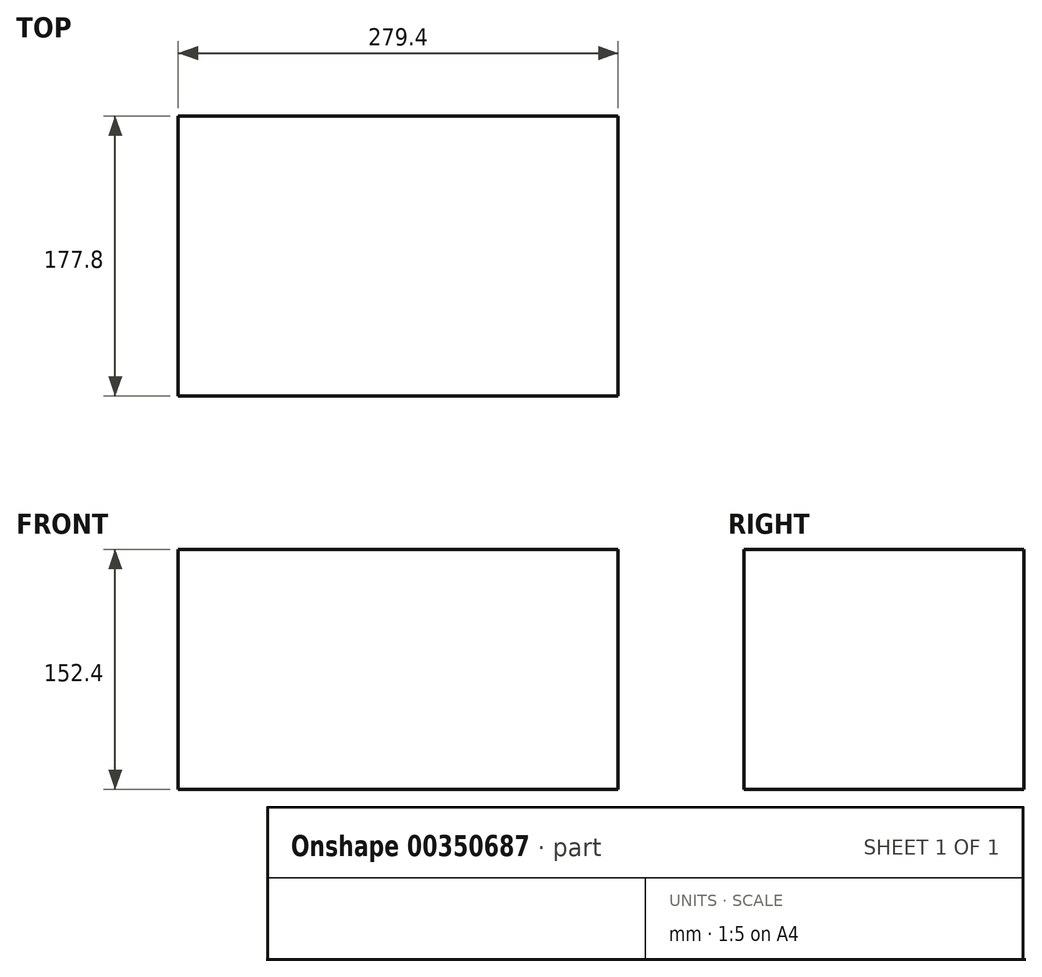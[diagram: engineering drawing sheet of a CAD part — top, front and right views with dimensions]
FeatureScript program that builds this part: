
annotation { "Feature Type Name" : "Feature", "Feature Type Description" : "" }
export const myFeature = defineFeature(function(context is Context, id is Id, definition is map)
    precondition{}
    {
        {
            var Q0;
            Q0=qCreatedBy(makeId("Front.planeOp"),FACE);
            var sketch = newSketch(context, id + "F0", { "sketchPlane" : qUnion([Q0])});
            skLineSegment(sketch, "E0.bottom", {"start": v(-139.7, 76.2) * mm, "end": v(139.7, 76.2) * mm});
            skLineSegment(sketch, "E0.top", {"start": v(-139.7, -76.2) * mm, "end": v(139.7, -76.2) * mm});
            skLineSegment(sketch, "E0.left", {"start": v(-139.7, 76.2) * mm, "end": v(-139.7, -76.2) * mm});
            skLineSegment(sketch, "E0.right", {"start": v(139.7, 76.2) * mm, "end": v(139.7, -76.2) * mm});
            skPoint(sketch, "E0.middle", {"position": v(0, 0) * mm});
            skSolve(sketch);
        }
        {
            var Q0;
            Q0=makeQuery(id+"F0.imprint","IMPRINT",FACE,{"disambiguationData":[TD([[makeQuery(id+"F0.imprint","IMPRINT",EDGE,{"derivedFrom":sQuery(id+"F0.wireOp",EDGE,"E0.bottom")}),-1.0]])]});
            extrude(context, id + "F1", {"entities" : qUnion([Q0]), "oppositeDirection" : true, "depth" : 177.8 * mm});
        }
    });
